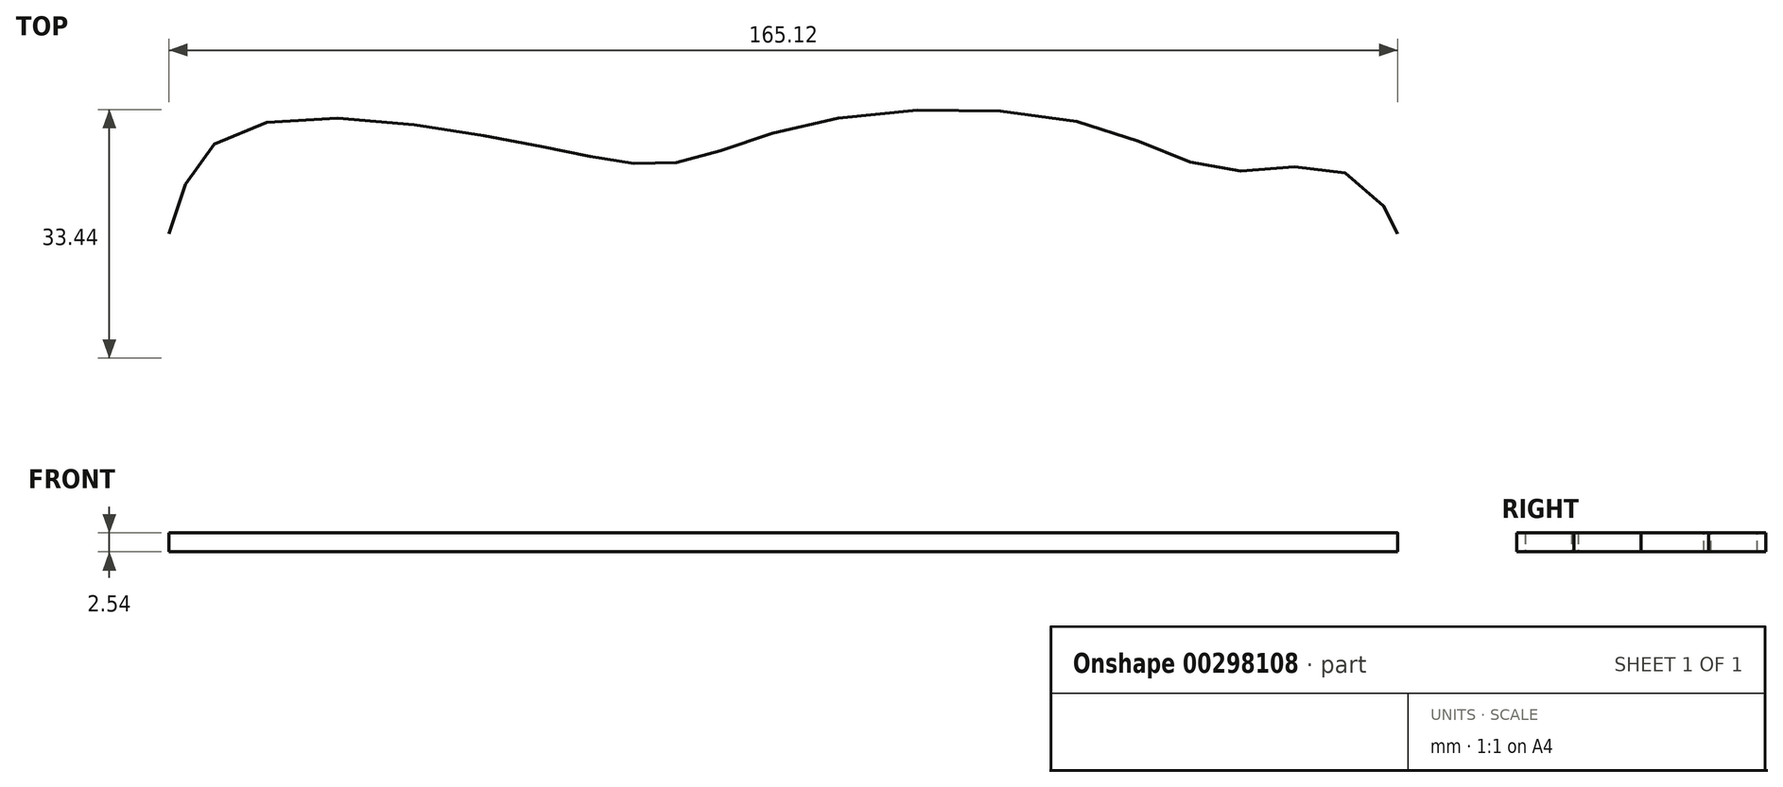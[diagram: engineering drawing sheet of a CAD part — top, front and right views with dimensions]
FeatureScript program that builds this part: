
annotation { "Feature Type Name" : "Feature", "Feature Type Description" : "" }
export const myFeature = defineFeature(function(context is Context, id is Id, definition is map)
    precondition{}
    {
        {
            var Q0;
            Q0=qCreatedBy(makeId("Top.planeOp"),FACE);
            var sketch = newSketch(context, id + "F0", { "sketchPlane" : qUnion([Q0])});
            skFitSpline(sketch, "E0", {"points": [v(-68.78, 0) * mm, v(-60.96, 13.19) * mm, v(-30.87, 13.97) * mm, v(-11.53, 10.26) * mm, v(0, 9.67) * mm, v(17, 14.75) * mm, v(54.7, 14.75) * mm, v(73.66, 8.5) * mm, v(90.27, 7.72) * mm, v(96.32, 0) * mm, v(95.93, 0) * mm], "startDerivative": vector(45.66, 160.82) * mm, "endDerivative": vector(-32.42, 11.33) * mm});
            skLineSegment(sketch, "E1", {"start": v(-68.78, 0) * mm, "end": v(96.32, 0) * mm});
            skSolve(sketch);
        }
        {
            var Q0;
            {var subQ0=sQuery(id+"F0.wireOp",EDGE,"E1");var subQ1=sQuery(id+"F0.wireOp",EDGE,"E0");var subQ2=makeQuery(id+"F0.imprint","INTERSECT",VERTEX,{"disambiguationData":[OD(0.0)],"derivedFrom":[subQ1,subQ0]});Q0=makeQuery(id+"F0.imprint","IMPRINT",FACE,{"disambiguationData":[TD([[makeQuery(id+"F0.imprint","IMPRINT",EDGE,{"disambiguationData":[TD([[subQ2,-1.0]])],"derivedFrom":subQ1}),-1.0]])]});}
            extrude(context, id + "F1", {"entities" : qUnion([Q0]), "depth" : 2.54 * mm});
        }
        {
            var Q0;
            Q0=makeQuery(id+"F1.opExtrude","SWEPT_BODY",BODY,{"disambiguationData":[OSD([sQuery(id+"F0.wireOp",EDGE,"E0"),sQuery(id+"F0.wireOp",EDGE,"E1")])]});
            var Q1;
            Q1=qCreatedBy(makeId("Front.planeOp"),FACE);
            mirror(context, id + "F2", {"operationType" : NewBodyOperationType.ADD, "entities" : qUnion([Q0]), "mirrorPlane" : qUnion([Q1])});
        }
    });
